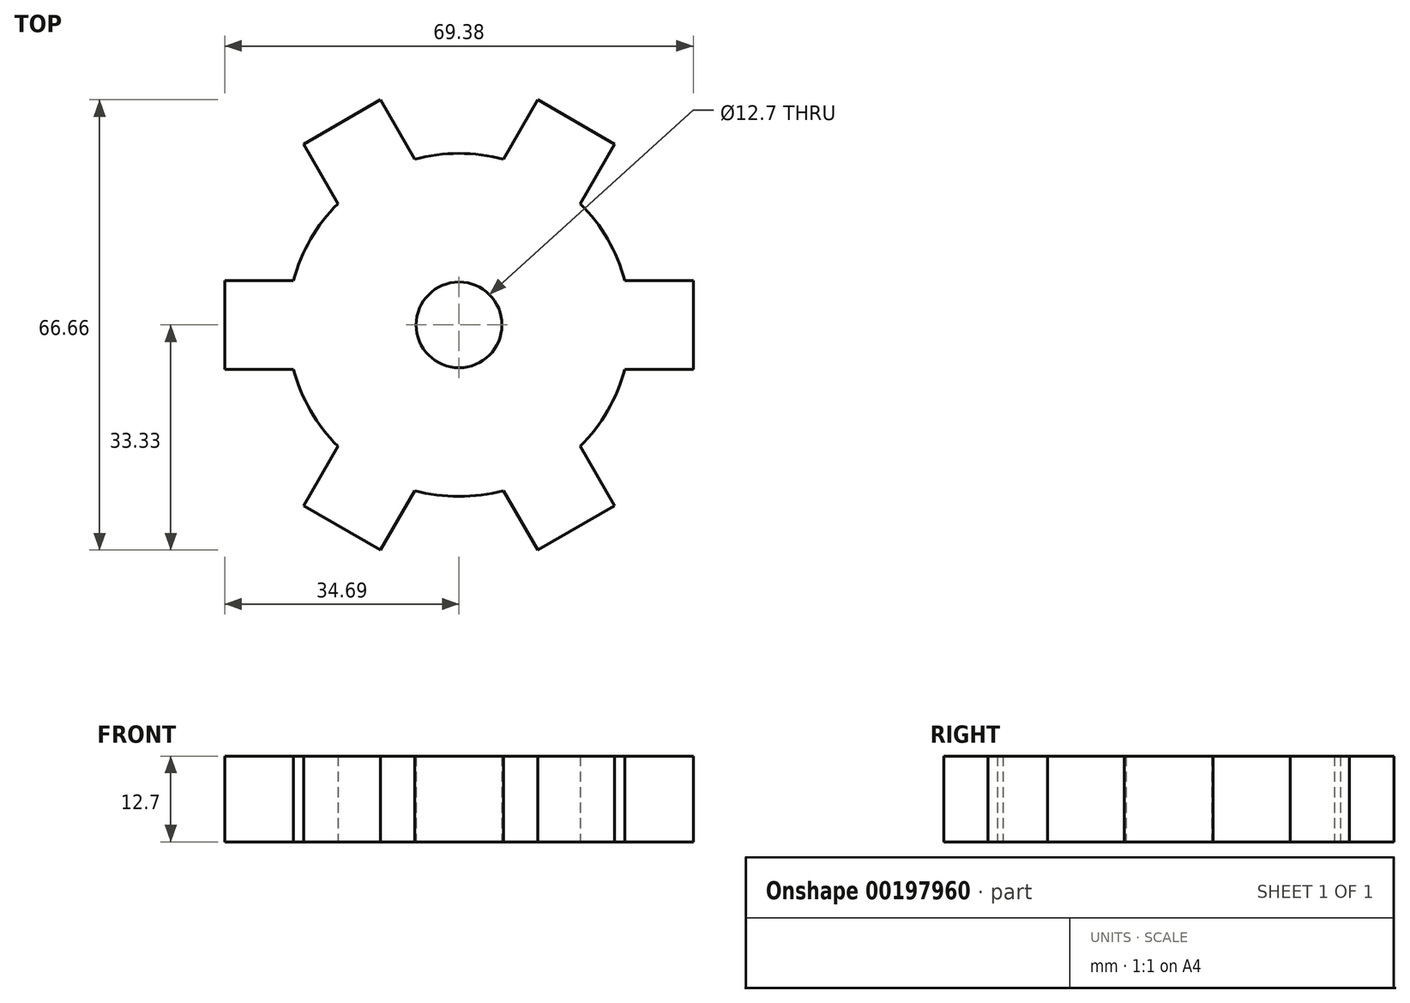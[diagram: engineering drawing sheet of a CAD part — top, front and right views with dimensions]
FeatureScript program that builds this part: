
annotation { "Feature Type Name" : "Feature", "Feature Type Description" : "" }
export const myFeature = defineFeature(function(context is Context, id is Id, definition is map)
    precondition{}
    {
        {
            var Q0;
            Q0=qCreatedBy(makeId("Top.planeOp"),FACE);
            var sketch = newSketch(context, id + "F0", { "sketchPlane" : qUnion([Q0])});
            skCircle(sketch, "E0", {"center": v(0, 0) * mm, "radius": 25.4 * mm});
            skSolve(sketch);
        }
        {
            var Q0;
            Q0=makeQuery(id+"F0.imprint","IMPRINT",FACE,{"disambiguationData":[TD([[makeQuery(id+"F0.imprint","IMPRINT",EDGE,{"derivedFrom":sQuery(id+"F0.wireOp",EDGE,"E0")}),1.0]])]});
            extrude(context, id + "F1", {"entities" : qUnion([Q0]), "depth" : 12.7 * mm});
        }
        {
            var Q0;
            Q0=makeQuery(id+"F1.opExtrude","CAP_FACE",FACE,{"disambiguationData":[OSD([sQuery(id+"F0.wireOp",EDGE,"E0")])],"isStart":true});
            var sketch = newSketch(context, id + "F2", { "sketchPlane" : qUnion([Q0])});
            skLineSegment(sketch, "E1", {"start": v(0, 0) * mm, "end": v(25.4, 0) * mm});
            skLineSegment(sketch, "E2", {"start": v(0, 0) * mm, "end": v(24.53, -6.57) * mm});
            skLineSegment(sketch, "E3", {"start": v(0, 0) * mm, "end": v(24.53, 6.57) * mm});
            skLineSegment(sketch, "E4", {"start": v(24.53, 6.57) * mm, "end": v(24.53, -6.57) * mm});
            skLineSegment(sketch, "E5.0", {"start": v(34.7, 6.57) * mm, "end": v(34.7, -6.57) * mm});
            skLineSegment(sketch, "E6", {"start": v(34.7, 6.57) * mm, "end": v(24.53, 6.57) * mm});
            skLineSegment(sketch, "E7", {"start": v(34.7, -6.57) * mm, "end": v(24.53, -6.57) * mm});
            skSolve(sketch);
        }
        {
            var Q0;
            Q0 = qSketchRegion(id + "F2", true);
            extrude(context, id + "F3", {"entities" : qUnion([Q0]), "operationType" : NewBodyOperationType.ADD, "oppositeDirection" : true, "depth" : 12.7 * mm});
        }
        {
            var Q0;
            Q0=qCreatedBy(makeId("Right.planeOp"),FACE);
            var sketch = newSketch(context, id + "F4", { "sketchPlane" : qUnion([Q0])});
            skLineSegment(sketch, "E8", {"start": v(0, 0) * mm, "end": v(0, 54.37) * mm});
            skSolve(sketch);
        }
        {
            var Q0;
            Q0=makeQuery(id+"F1.opExtrude","SWEPT_BODY",BODY,{"disambiguationData":[OSD([sQuery(id+"F0.wireOp",EDGE,"E0")])]});
            var Q1;
            Q1=sQuery(id+"F4.wireOp",EDGE,"E8");
            circularPattern(context, id + "F5", {"operationType" : NewBodyOperationType.ADD, "entities" : qUnion([Q0]), "axis" : qUnion([Q1]), "angle" : 360 * degree, "instanceCount" : 6, "equalSpace" : true});
        }
        {
            var Q0;
            {var subQ0=makeQuery(id+"F3.boolean.opBoolean","MERGE",FACE,{"derivedFrom":[makeQuery(id+"F1.opExtrude","CAP_FACE",FACE,{"disambiguationData":[OSD([sQuery(id+"F0.wireOp",EDGE,"E0")])],"isStart":true}),makeQuery(id+"F3.opExtrude","CAP_FACE",FACE,{"disambiguationData":[OSD([sQuery(id+"F2.wireOp",EDGE,"E2"),sQuery(id+"F2.wireOp",EDGE,"E3"),sQuery(id+"F2.wireOp",EDGE,"E5.0"),sQuery(id+"F2.wireOp",EDGE,"E6"),sQuery(id+"F2.wireOp",EDGE,"E7")])],"isStart":true})]});Q0=makeQuery(id+"F5.boolean.opBoolean","MERGE",FACE,{"derivedFrom":[subQ0,makeQuery(id+"F5.opPattern","COPY",FACE,{"derivedFrom":subQ0,"instanceName":"1"}),makeQuery(id+"F5.opPattern","COPY",FACE,{"derivedFrom":subQ0,"instanceName":"2"}),makeQuery(id+"F5.opPattern","COPY",FACE,{"derivedFrom":subQ0,"instanceName":"3"}),makeQuery(id+"F5.opPattern","COPY",FACE,{"derivedFrom":subQ0,"instanceName":"4"}),makeQuery(id+"F5.opPattern","COPY",FACE,{"derivedFrom":subQ0,"instanceName":"5"})]});}
            var sketch = newSketch(context, id + "F6", { "sketchPlane" : qUnion([Q0])});
            skCircle(sketch, "E9", {"center": v(0, 0) * mm, "radius": 6.35 * mm});
            skSolve(sketch);
        }
        {
            var Q0;
            Q0 = qSketchRegion(id + "F6", true);
            extrude(context, id + "F7", {"entities" : qUnion([Q0]), "operationType" : NewBodyOperationType.REMOVE, "endBound" : BoundingType.THROUGH_ALL, "oppositeDirection" : true, "depth" : 25.4 * mm});
        }
    });
